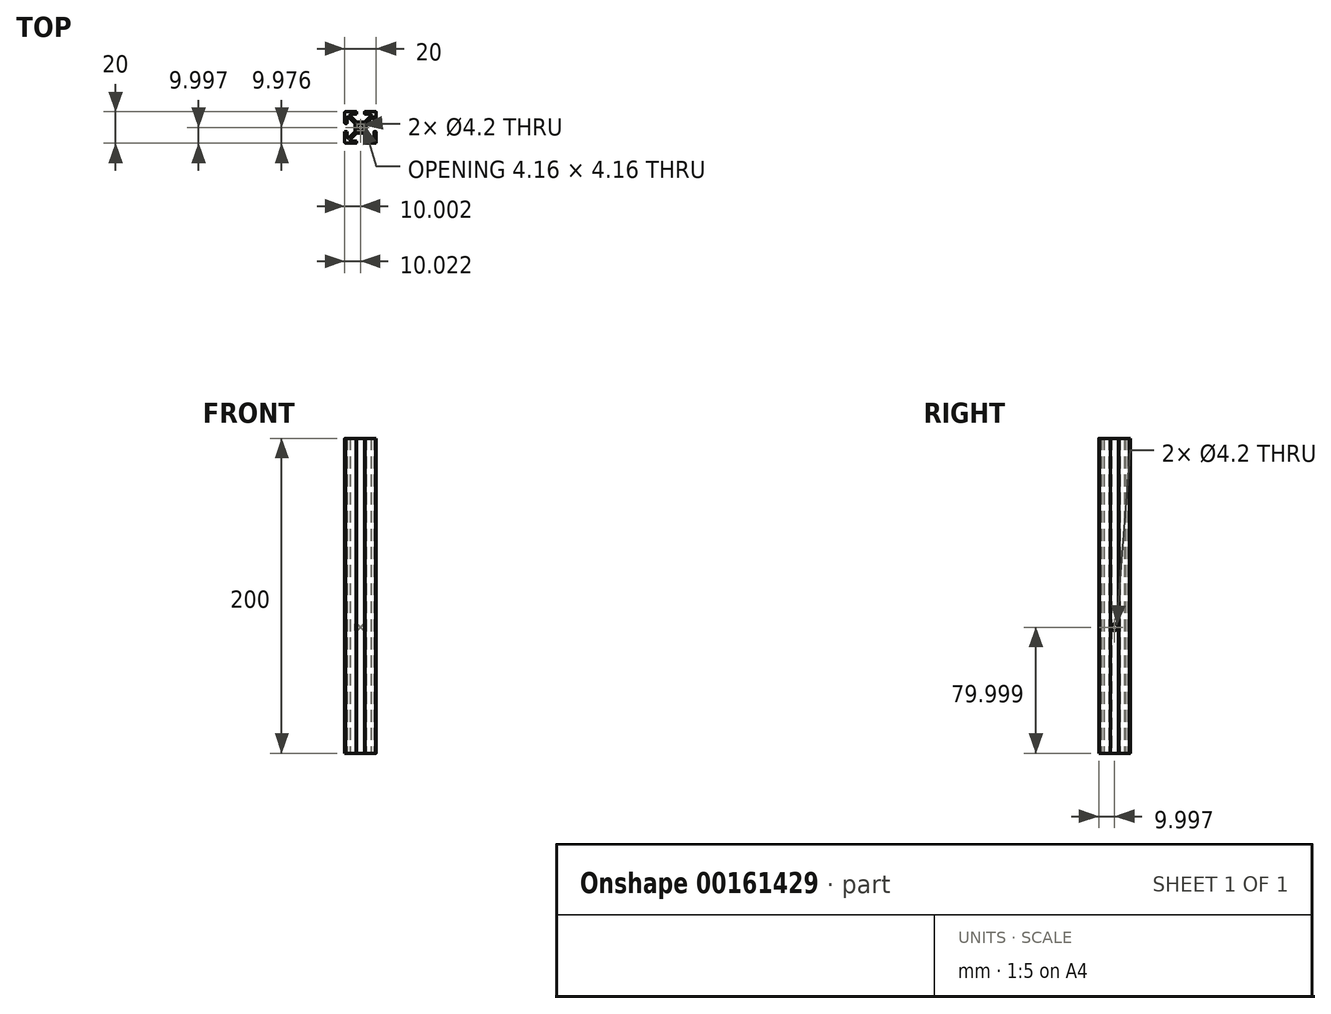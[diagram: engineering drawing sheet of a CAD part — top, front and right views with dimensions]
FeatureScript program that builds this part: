
annotation { "Feature Type Name" : "Feature", "Feature Type Description" : "" }
export const myFeature = defineFeature(function(context is Context, id is Id, definition is map)
    precondition{}
    {
        {
            var Q0;
            Q0=qCreatedBy(makeId("Top.planeOp"),FACE);
            var sketch = newSketch(context, id + "F0", { "sketchPlane" : qUnion([Q0])});
            skLineSegment(sketch, "E0.top", {"start": v(-10.81, -9.52) * mm, "end": v(-10.8, -9.52) * mm});
            skLineSegment(sketch, "E0.right", {"start": v(9.19, 10.48) * mm, "end": v(9.19, 10.47) * mm});
            skLineSegment(sketch, "E1.bottom", {"start": v(-3.56, 10.48) * mm, "end": v(-10.3, 10.48) * mm});
            skLineSegment(sketch, "E1.top", {"start": v(8.7, -9.52) * mm, "end": v(1.95, -9.52) * mm});
            skLineSegment(sketch, "E1.left", {"start": v(9.2, 9.98) * mm, "end": v(9.2, 3.23) * mm});
            skLineSegment(sketch, "E1.right", {"start": v(-10.8, -2.27) * mm, "end": v(-10.8, -9.02) * mm});
            skLineSegment(sketch, "E2", {"start": v(-10.8, 10.48) * mm, "end": v(-10.3, 9.98) * mm});
            skLineSegment(sketch, "E3", {"start": v(9.2, 10.48) * mm, "end": v(8.7, 9.98) * mm});
            skCircle(sketch, "E4", {"center": v(-0.8, 0.48) * mm, "radius": 2.1 * mm});
            skLineSegment(sketch, "E5.left", {"start": v(-3.3, 10.23) * mm, "end": v(-3.3, 9.23) * mm});
            skLineSegment(sketch, "E5.right", {"start": v(1.7, 10.23) * mm, "end": v(1.7, 9.23) * mm});
            skLineSegment(sketch, "E6", {"start": v(-4.3, 2.81) * mm, "end": v(-4.3, -1.86) * mm});
            skLineSegment(sketch, "E7", {"start": v(2.7, 2.81) * mm, "end": v(2.7, -1.86) * mm});
            skLineSegment(sketch, "E8", {"start": v(-7.04, -8.02) * mm, "end": v(-3.56, -8.02) * mm});
            skLineSegment(sketch, "E9", {"start": v(-9.3, -2.27) * mm, "end": v(-9.3, -5.76) * mm});
            skLineSegment(sketch, "E10", {"start": v(7.7, 6.7) * mm, "end": v(7.7, 3.23) * mm});
            skLineSegment(sketch, "E11", {"start": v(-7.04, 8.98) * mm, "end": v(-3.56, 8.98) * mm});
            skLineSegment(sketch, "E12.bottom", {"start": v(7.94, 2.98) * mm, "end": v(8.94, 2.98) * mm});
            skLineSegment(sketch, "E12.top", {"start": v(-10.56, -2.02) * mm, "end": v(-9.56, -2.02) * mm});
            skPoint(sketch, "E12.middle", {"position": v(9.2, 0.48) * mm});
            skLineSegment(sketch, "E13", {"start": v(-7.4, 8.12) * mm, "end": v(-3.32, 4.05) * mm});
            skLineSegment(sketch, "E14", {"start": v(1.7, -3.1) * mm, "end": v(5.78, -7.17) * mm});
            skLineSegment(sketch, "E15", {"start": v(5.78, 8.12) * mm, "end": v(1.7, 4.05) * mm});
            skLineSegment(sketch, "E16", {"start": v(-3.32, -3.1) * mm, "end": v(-7.4, -7.17) * mm});
            skArc(sketch, "E17.filletArc", {"start": v(-7.04, 8.98) * mm, "mid": v(-7.5, 8.67) * mm, "end": v(-7.4, 8.12) * mm});
            skPoint(sketch, "E18.newPointB", {"position": v(9.2, 8.98) * mm});
            skArc(sketch, "E18.filletArc", {"start": v(5.78, 8.12) * mm, "mid": v(5.89, 8.67) * mm, "end": v(5.42, 8.98) * mm});
            skArc(sketch, "E19.filletArc", {"start": v(7.7, 6.7) * mm, "mid": v(7.38, 7.17) * mm, "end": v(6.84, 7.06) * mm});
            skArc(sketch, "E20.filletArc", {"start": v(6.84, -6.1) * mm, "mid": v(7.38, -6.22) * mm, "end": v(7.7, -5.76) * mm});
            skArc(sketch, "E21.filletArc", {"start": v(5.42, -8.02) * mm, "mid": v(5.89, -7.71) * mm, "end": v(5.78, -7.17) * mm});
            skArc(sketch, "E22.filletArc", {"start": v(-7.4, -7.17) * mm, "mid": v(-7.5, -7.71) * mm, "end": v(-7.04, -8.02) * mm});
            skArc(sketch, "E23.filletArc", {"start": v(-9.3, -5.76) * mm, "mid": v(-9, -6.22) * mm, "end": v(-8.45, -6.1) * mm});
            skArc(sketch, "E24.filletArc", {"start": v(-8.45, 7.06) * mm, "mid": v(-9.02, 7.16) * mm, "end": v(-9.3, 6.65) * mm});
            skPoint(sketch, "E25.visualSharp", {"position": v(-10.8, 10.48) * mm});
            skArc(sketch, "E25.filletArc", {"start": v(-10.3, 10.48) * mm, "mid": v(-10.66, 10.33) * mm, "end": v(-10.8, 9.98) * mm});
            skPoint(sketch, "E26.visualSharp", {"position": v(9.2, 10.48) * mm});
            skArc(sketch, "E26.filletArc", {"start": v(9.2, 9.98) * mm, "mid": v(9.05, 10.33) * mm, "end": v(8.7, 10.48) * mm});
            skPoint(sketch, "E27.visualSharp", {"position": v(9.2, -9.52) * mm});
            skArc(sketch, "E27.filletArc", {"start": v(8.7, -9.52) * mm, "mid": v(9.05, -9.38) * mm, "end": v(9.2, -9.02) * mm});
            skPoint(sketch, "E28.visualSharp", {"position": v(-10.8, -9.52) * mm});
            skArc(sketch, "E28.filletArc", {"start": v(-10.8, -9.02) * mm, "mid": v(-10.66, -9.38) * mm, "end": v(-10.3, -9.52) * mm});
            skArc(sketch, "E29.filletArc", {"start": v(-3.56, 8.98) * mm, "mid": v(-3.38, 9.05) * mm, "end": v(-3.3, 9.23) * mm});
            skArc(sketch, "E30.filletArc", {"start": v(-9.3, -2.27) * mm, "mid": v(-9.38, -2.1) * mm, "end": v(-9.56, -2.02) * mm});
            skArc(sketch, "E31.filletArc", {"start": v(-3.3, 10.23) * mm, "mid": v(-3.38, 10.4) * mm, "end": v(-3.56, 10.48) * mm});
            skLineSegment(sketch, "E32", {"start": v(1.94, 10.48) * mm, "end": v(8.7, 10.48) * mm});
            skLineSegment(sketch, "E33", {"start": v(5.42, 8.98) * mm, "end": v(1.94, 8.98) * mm});
            skLineSegment(sketch, "E34", {"start": v(-9.3, 6.65) * mm, "end": v(-9.3, 3.23) * mm});
            skLineSegment(sketch, "E35", {"start": v(7.94, -2.02) * mm, "end": v(8.94, -2.02) * mm});
            skPoint(sketch, "E36.visualSharp", {"position": v(1.7, 8.98) * mm});
            skArc(sketch, "E36.filletArc", {"start": v(1.7, 9.23) * mm, "mid": v(1.77, 9.05) * mm, "end": v(1.94, 8.98) * mm});
            skPoint(sketch, "E37.visualSharp", {"position": v(1.7, 10.48) * mm});
            skArc(sketch, "E37.filletArc", {"start": v(1.94, 10.48) * mm, "mid": v(1.77, 10.4) * mm, "end": v(1.7, 10.23) * mm});
            skPoint(sketch, "E38.newPointB", {"position": v(-10.8, 2.98) * mm});
            skArc(sketch, "E38.filletArc", {"start": v(7.7, 3.23) * mm, "mid": v(7.77, 3.05) * mm, "end": v(7.94, 2.98) * mm});
            skLineSegment(sketch, "E39", {"start": v(7.7, -2.27) * mm, "end": v(7.7, -5.76) * mm});
            skPoint(sketch, "E40.visualSharp", {"position": v(7.7, -2.02) * mm});
            skArc(sketch, "E40.filletArc", {"start": v(7.94, -2.02) * mm, "mid": v(7.77, -2.1) * mm, "end": v(7.7, -2.27) * mm});
            skArc(sketch, "E41.filletArc", {"start": v(8.94, 2.98) * mm, "mid": v(9.12, 3.05) * mm, "end": v(9.2, 3.23) * mm});
            skLineSegment(sketch, "E42", {"start": v(9.2, -2.27) * mm, "end": v(9.2, -9.02) * mm});
            skPoint(sketch, "E43.visualSharp", {"position": v(9.2, -2.02) * mm});
            skArc(sketch, "E43.filletArc", {"start": v(9.2, -2.27) * mm, "mid": v(9.12, -2.1) * mm, "end": v(8.94, -2.02) * mm});
            skLineSegment(sketch, "E44", {"start": v(-9.56, 2.98) * mm, "end": v(-10.56, 2.98) * mm});
            skPoint(sketch, "E45.visualSharp", {"position": v(-9.3, 2.98) * mm});
            skArc(sketch, "E45.filletArc", {"start": v(-9.56, 2.98) * mm, "mid": v(-9.38, 3.05) * mm, "end": v(-9.3, 3.23) * mm});
            skPoint(sketch, "E46.newPointA", {"position": v(-10.8, -2.02) * mm});
            skArc(sketch, "E46.filletArc", {"start": v(-10.56, -2.02) * mm, "mid": v(-10.73, -2.1) * mm, "end": v(-10.8, -2.27) * mm});
            skLineSegment(sketch, "E47", {"start": v(-10.8, 3.23) * mm, "end": v(-10.8, 9.98) * mm});
            skArc(sketch, "E48.filletArc", {"start": v(-10.8, 3.23) * mm, "mid": v(-10.73, 3.05) * mm, "end": v(-10.56, 2.98) * mm});
            skPoint(sketch, "E49.newPointB", {"position": v(-3.3, 2.98) * mm});
            skLineSegment(sketch, "E50", {"start": v(6.84, -6.1) * mm, "end": v(2.77, -2.04) * mm});
            skPoint(sketch, "E50.endSnap0", {"position": v(2.7, -0.27) * mm});
            skPoint(sketch, "E51.newPointA", {"position": v(2.7, -1.96) * mm});
            skPoint(sketch, "E51.newPointB", {"position": v(2.7, -9.52) * mm});
            skArc(sketch, "E51.filletArc", {"start": v(2.7, -1.86) * mm, "mid": v(2.71, -1.95) * mm, "end": v(2.77, -2.04) * mm});
            skLineSegment(sketch, "E52", {"start": v(-3.14, -3.02) * mm, "end": v(1.53, -3.02) * mm});
            skArc(sketch, "E53.filletArc", {"start": v(1.7, -3.1) * mm, "mid": v(1.62, -3.04) * mm, "end": v(1.53, -3.02) * mm});
            skArc(sketch, "E54.filletArc", {"start": v(-3.14, -3.02) * mm, "mid": v(-3.24, -3.04) * mm, "end": v(-3.32, -3.1) * mm});
            skLineSegment(sketch, "E55", {"start": v(-8.45, -6.1) * mm, "end": v(-4.38, -2.04) * mm});
            skLineSegment(sketch, "E56", {"start": v(-8.45, 7.06) * mm, "end": v(-4.38, 2.99) * mm});
            skArc(sketch, "E57.filletArc", {"start": v(-4.3, 2.81) * mm, "mid": v(-4.33, 2.9) * mm, "end": v(-4.38, 2.99) * mm});
            skArc(sketch, "E58.filletArc", {"start": v(-4.38, -2.04) * mm, "mid": v(-4.33, -1.95) * mm, "end": v(-4.3, -1.86) * mm});
            skLineSegment(sketch, "E59", {"start": v(6.84, 7.06) * mm, "end": v(2.77, 2.99) * mm});
            skPoint(sketch, "E60.newPointB", {"position": v(2.7, 8.98) * mm});
            skArc(sketch, "E60.filletArc", {"start": v(2.77, 2.99) * mm, "mid": v(2.71, 2.9) * mm, "end": v(2.7, 2.81) * mm});
            skLineSegment(sketch, "E61", {"start": v(-3.14, 3.98) * mm, "end": v(1.53, 3.98) * mm});
            skArc(sketch, "E62.filletArc", {"start": v(-3.32, 4.05) * mm, "mid": v(-3.24, 4) * mm, "end": v(-3.14, 3.98) * mm});
            skArc(sketch, "E63.filletArc", {"start": v(1.53, 3.98) * mm, "mid": v(1.62, 4) * mm, "end": v(1.7, 4.05) * mm});
            skPoint(sketch, "E64.orphan", {"position": v(-3.3, 10.48) * mm});
            skPoint(sketch, "E65.orphan", {"position": v(-0.8, 10.48) * mm});
            skPoint(sketch, "E66.orphan", {"position": v(-10.8, 0.48) * mm});
            skLineSegment(sketch, "E67.trimOffspring", {"start": v(8.7, -9.02) * mm, "end": v(9.2, -9.52) * mm});
            skLineSegment(sketch, "E68.trimOffspring", {"start": v(-10.3, -9.02) * mm, "end": v(-10.8, -9.52) * mm});
            skPoint(sketch, "E69.trimOffspring.end.orphan", {"position": v(-0.8, -9.52) * mm});
            skLineSegment(sketch, "E70", {"start": v(1.7, 9.73) * mm, "end": v(1.7, 9.15) * mm});
            skPoint(sketch, "E70.startSnap0", {"position": v(1.7, 9.73) * mm});
            skLineSegment(sketch, "E71", {"start": v(-3.3, 9.73) * mm, "end": v(-3.3, 9.23) * mm});
            skPoint(sketch, "E72.start.orphan", {"position": v(-3.14, -8.02) * mm});
            skLineSegment(sketch, "E73.trimOffspring", {"start": v(1.95, -8.02) * mm, "end": v(5.42, -8.02) * mm});
            skLineSegment(sketch, "E74.trimOffspring", {"start": v(-3.56, -9.52) * mm, "end": v(-10.3, -9.52) * mm});
            skLineSegment(sketch, "E75.trimOffspring", {"start": v(1.7, -8.27) * mm, "end": v(1.7, -9.27) * mm});
            skLineSegment(sketch, "E76.trimOffspring", {"start": v(-3.3, -8.27) * mm, "end": v(-3.3, -9.27) * mm});
            skArc(sketch, "E77.filletArc", {"start": v(-3.3, -8.27) * mm, "mid": v(-3.38, -8.1) * mm, "end": v(-3.56, -8.02) * mm});
            skPoint(sketch, "E78.visualSharp", {"position": v(1.7, -8.02) * mm});
            skArc(sketch, "E78.filletArc", {"start": v(1.95, -8.02) * mm, "mid": v(1.78, -8.1) * mm, "end": v(1.7, -8.27) * mm});
            skPoint(sketch, "E79.visualSharp", {"position": v(-3.3, -9.52) * mm});
            skArc(sketch, "E79.filletArc", {"start": v(-3.56, -9.52) * mm, "mid": v(-3.38, -9.45) * mm, "end": v(-3.3, -9.27) * mm});
            skPoint(sketch, "E80.visualSharp", {"position": v(1.7, -9.52) * mm});
            skArc(sketch, "E80.filletArc", {"start": v(1.7, -9.27) * mm, "mid": v(1.78, -9.45) * mm, "end": v(1.95, -9.52) * mm});
            skLineSegment(sketch, "E81.trimOffspring", {"start": v(9.19, -2.23) * mm, "end": v(9.19, -9.08) * mm});
            skLineSegment(sketch, "E82.trimOffspring", {"start": v(1.94, -9.52) * mm, "end": v(8.71, -9.52) * mm});
            skLineSegment(sketch, "E83", {"start": v(-10.8, -9.02) * mm, "end": v(-10.8, -2.27) * mm});
            skLineSegment(sketch, "E84", {"start": v(-10.8, 9.98) * mm, "end": v(-10.8, 3.23) * mm});
            skLineSegment(sketch, "E85.trimOffspring", {"start": v(9.19, 10.04) * mm, "end": v(9.19, 3.19) * mm});
            skLineSegment(sketch, "E86.trimOffspring", {"start": v(9.19, -9.52) * mm, "end": v(9.19, -9.52) * mm});
            skLineSegment(sketch, "E87.trimOffspring", {"start": v(-10.33, -9.52) * mm, "end": v(-3.54, -9.52) * mm});
            skSolve(sketch);
        }
        {
            var Q0;
            Q0=makeQuery(id+"F0.imprint","IMPRINT",FACE,{"disambiguationData":[TD([[makeQuery(id+"F0.imprint","IMPRINT",EDGE,{"derivedFrom":sQuery(id+"F0.wireOp",EDGE,"E4")}),-1.0]])]});
            extrude(context, id + "F1", {"entities" : qUnion([Q0]), "depth" : 200 * mm});
        }
        {
            var Q0;
            Q0=makeQuery(id+"F1.opExtrude","SWEPT_FACE",FACE,{"disambiguationData":[OSD([sQuery(id+"F0.wireOp",EDGE,"E7")])]});
            var sketch = newSketch(context, id + "F2", { "sketchPlane" : qUnion([Q0])});
            skPoint(sketch, "E88", {"position": v(0.48, 80) * mm});
            skPoint(sketch, "E89.orphan", {"position": v(0.48, 200) * mm});
            skPoint(sketch, "E90.orphan", {"position": v(2.81, 80) * mm});
            skPoint(sketch, "E91.start.orphan", {"position": v(-1.86, 80) * mm});
            skCircle(sketch, "E92", {"center": v(0.48, 80) * mm, "radius": 2.1 * mm});
            skSolve(sketch);
        }
        {
            var Q0;
            Q0 = qSketchRegion(id + "F2", true);
            extrude(context, id + "F3", {"entities" : qUnion([Q0]), "operationType" : NewBodyOperationType.REMOVE, "oppositeDirection" : true, "depth" : 7 * mm});
        }
    });
